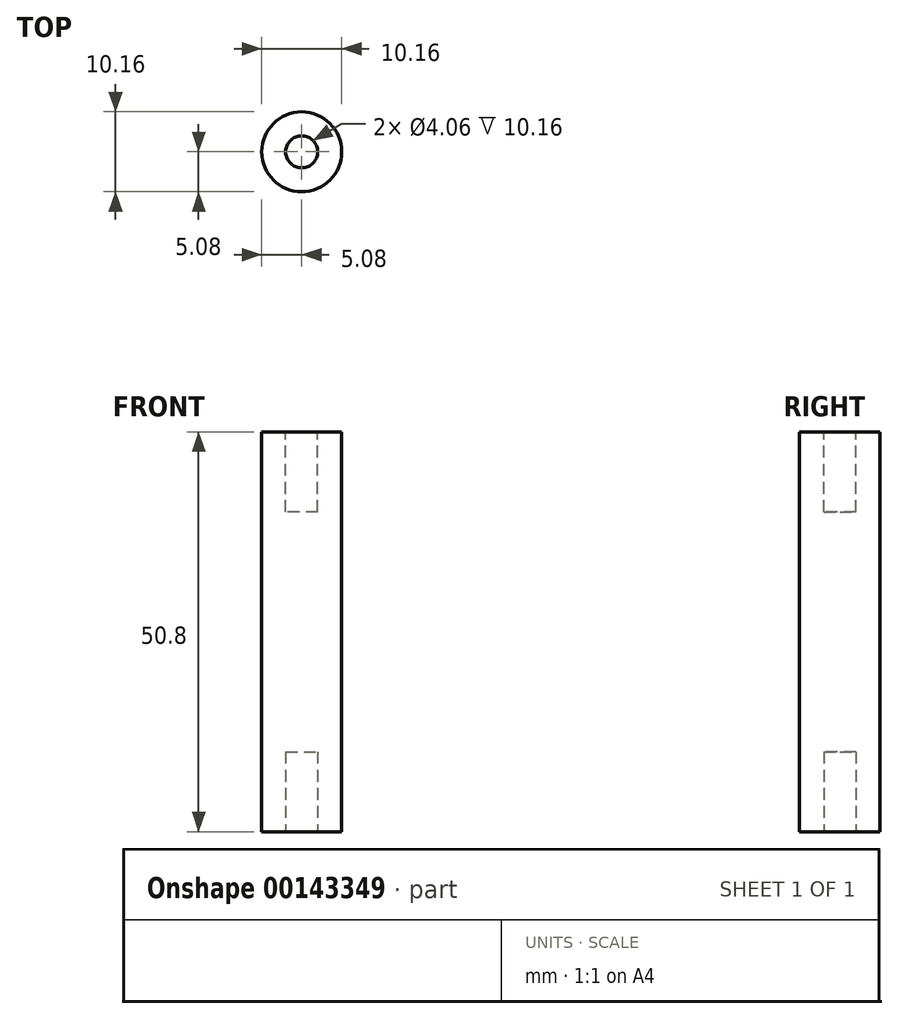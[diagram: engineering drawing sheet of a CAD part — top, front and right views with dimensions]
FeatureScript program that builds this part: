
annotation { "Feature Type Name" : "Feature", "Feature Type Description" : "" }
export const myFeature = defineFeature(function(context is Context, id is Id, definition is map)
    precondition{}
    {
        {
            var Q0;
            Q0=qCreatedBy(makeId("Top.planeOp"),FACE);
            var sketch = newSketch(context, id + "F0", { "sketchPlane" : qUnion([Q0])});
            skCircle(sketch, "E0", {"center": v(0, 0) * mm, "radius": 5.08 * mm});
            skSolve(sketch);
        }
        {
            var Q0;
            Q0=makeQuery(id+"F0.imprint","IMPRINT",FACE,{"disambiguationData":[TD([[makeQuery(id+"F0.imprint","IMPRINT",EDGE,{"derivedFrom":sQuery(id+"F0.wireOp",EDGE,"E0")}),1.0]])]});
            var Q1;
            Q1=sQuery(id+"F0.wireOp",EDGE,"E0");
            extrude(context, id + "F1", {"entities" : qUnion([Q0]), "surfaceEntities" : qUnion([Q1]), "depth" : 50.8 * mm});
        }
        {
            var Q0;
            Q0=makeQuery(id+"F1.opExtrude","CAP_FACE",FACE,{"disambiguationData":[OSD([sQuery(id+"F0.wireOp",EDGE,"E0")])],"isStart":false});
            var sketch = newSketch(context, id + "F2", { "sketchPlane" : qUnion([Q0])});
            skCircle(sketch, "E1", {"center": v(0, 0) * mm, "radius": 2.03 * mm});
            skSolve(sketch);
        }
        {
            var Q0;
            Q0 = qSketchRegion(id + "F2", true);
            extrude(context, id + "F3", {"entities" : qUnion([Q0]), "operationType" : NewBodyOperationType.REMOVE, "oppositeDirection" : true, "depth" : 10.16 * mm});
        }
        {
            var Q0;
            Q0=makeQuery(id+"F1.opExtrude","CAP_FACE",FACE,{"disambiguationData":[OSD([sQuery(id+"F0.wireOp",EDGE,"E0")])],"isStart":true});
            var sketch = newSketch(context, id + "F4", { "sketchPlane" : qUnion([Q0])});
            skCircle(sketch, "E2", {"center": v(0, 0) * mm, "radius": 2.03 * mm});
            skSolve(sketch);
        }
        {
            var Q0;
            Q0 = qSketchRegion(id + "F4", true);
            extrude(context, id + "F5", {"entities" : qUnion([Q0]), "operationType" : NewBodyOperationType.REMOVE, "oppositeDirection" : true, "depth" : 10.16 * mm});
        }
    });
